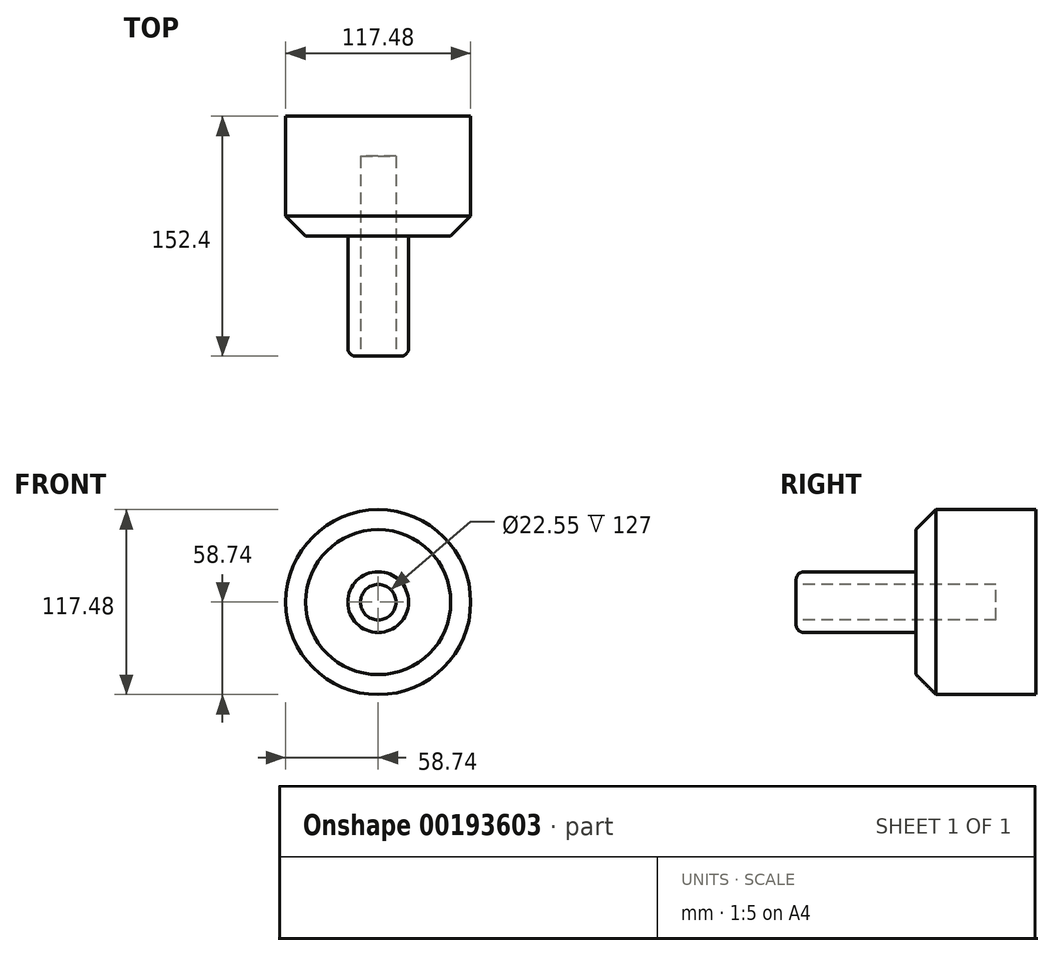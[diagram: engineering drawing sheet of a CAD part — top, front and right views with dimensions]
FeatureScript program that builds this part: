
annotation { "Feature Type Name" : "Feature", "Feature Type Description" : "" }
export const myFeature = defineFeature(function(context is Context, id is Id, definition is map)
    precondition{}
    {
        {
            var Q0;
            Q0=qCreatedBy(makeId("Front.planeOp"),FACE);
            var sketch = newSketch(context, id + "F0", { "sketchPlane" : qUnion([Q0])});
            skCircle(sketch, "E0", {"center": v(0, 0) * mm, "radius": 58.74 * mm});
            skSolve(sketch);
        }
        {
            var Q0;
            Q0=makeQuery(id+"F0.imprint","IMPRINT",FACE,{"disambiguationData":[TD([[makeQuery(id+"F0.imprint","IMPRINT",EDGE,{"derivedFrom":sQuery(id+"F0.wireOp",EDGE,"E0")}),1.0]])]});
            var sketch = newSketch(context, id + "F1", { "sketchPlane" : qUnion([Q0])});
            skSolve(sketch);
        }
        {
            var Q0;
            Q0 = qSketchRegion(id + "F1", true);
            var Q1;
            Q1=makeQuery(id+"F0.imprint","IMPRINT",FACE,{"disambiguationData":[TD([[makeQuery(id+"F0.imprint","IMPRINT",EDGE,{"derivedFrom":sQuery(id+"F0.wireOp",EDGE,"E0")}),1.0]])]});
            extrude(context, id + "F2", {"entities" : qUnion([Q0, Q1]), "depth" : 76.2 * mm});
        }
        {
            var Q0;
            Q0=makeQuery(id+"F2.opExtrude","CAP_FACE",FACE,{"disambiguationData":[OSD([sQuery(id+"F0.wireOp",EDGE,"E0")])],"isStart":false});
            var sketch = newSketch(context, id + "F3", { "sketchPlane" : qUnion([Q0])});
            skCircle(sketch, "E1", {"center": v(0, 0) * mm, "radius": 19.3 * mm});
            skSolve(sketch);
        }
        {
            var Q0;
            Q0=makeQuery(id+"F3.imprint","IMPRINT",FACE,{"disambiguationData":[TD([[makeQuery(id+"F3.imprint","IMPRINT",EDGE,{"derivedFrom":sQuery(id+"F3.wireOp",EDGE,"E1")}),1.0]])]});
            extrude(context, id + "F4", {"entities" : qUnion([Q0]), "operationType" : NewBodyOperationType.ADD, "depth" : 76.2 * mm});
        }
        {
            var Q0;
            Q0=qCreatedBy(makeId("Front.planeOp"),FACE);
            var sketch = newSketch(context, id + "F5", { "sketchPlane" : qUnion([Q0])});
            skCircle(sketch, "E2", {"center": v(0, 0) * mm, "radius": 9.66 * mm});
            skSolve(sketch);
        }
        {
            var Q0;
            Q0=qCreatedBy(makeId("Front.planeOp"),FACE);
            var sketch = newSketch(context, id + "F6", { "sketchPlane" : qUnion([Q0])});
            skCircle(sketch, "E3", {"center": v(0, 0) * mm, "radius": 9.7 * mm});
            skSolve(sketch);
        }
        {
            var Q0;
            Q0 = qSketchRegion(id + "F6", true);
            extrude(context, id + "F7", {"entities" : qUnion([Q0]), "operationType" : NewBodyOperationType.REMOVE, "oppositeDirection" : true, "depth" : 76.2 * mm});
        }
        {
            var Q0;
            Q0=makeQuery(id+"F5.imprint","IMPRINT",FACE,{"disambiguationData":[TD([[makeQuery(id+"F5.imprint","IMPRINT",EDGE,{"derivedFrom":sQuery(id+"F5.wireOp",EDGE,"E2")}),1.0]])]});
            var Q1;
            Q1=sQuery(id+"F5.wireOp",EDGE,"E2");
            extrude(context, id + "F8", {"entities" : qUnion([Q0]), "operationType" : NewBodyOperationType.REMOVE, "surfaceEntities" : qUnion([Q1]), "oppositeDirection" : true, "depth" : 127 * mm});
        }
        {
            var Q0;
            Q0=makeQuery(id+"F4.opExtrude","CAP_FACE",FACE,{"disambiguationData":[OSD([sQuery(id+"F3.wireOp",EDGE,"E1")])],"isStart":false});
            var sketch = newSketch(context, id + "F9", { "sketchPlane" : qUnion([Q0])});
            skCircle(sketch, "E4", {"center": v(0, 0) * mm, "radius": 11.27 * mm});
            skSolve(sketch);
        }
        {
            var Q0;
            Q0=makeQuery(id+"F9.imprint","IMPRINT",FACE,{"disambiguationData":[TD([[makeQuery(id+"F9.imprint","IMPRINT",EDGE,{"derivedFrom":sQuery(id+"F9.wireOp",EDGE,"E4")}),1.0]])]});
            var Q1;
            Q1=sQuery(id+"F9.wireOp",EDGE,"E4");
            extrude(context, id + "F10", {"entities" : qUnion([Q0]), "operationType" : NewBodyOperationType.REMOVE, "surfaceEntities" : qUnion([Q1]), "oppositeDirection" : true, "depth" : 127 * mm});
        }
        {
            var Q0;
            Q0=makeQuery(id+"F4.opExtrude","CAP_EDGE",EDGE,{"disambiguationData":[OSD([sQuery(id+"F3.wireOp",EDGE,"E1")])],"isStart":false});
            fillet(context, id + "F11", {"entities" : qUnion([Q0]), "radius" : 5.08 * mm, "tangentPropagation" : true, "allowEdgeOverflow" : false});
        }
        {
            var Q0;
            Q0=makeQuery(id+"F2.opExtrude","CAP_EDGE",EDGE,{"disambiguationData":[OSD([sQuery(id+"F0.wireOp",EDGE,"E0")])],"isStart":false});
            chamfer(context, id + "F12", {"entities" : qUnion([Q0]), "width" : 12.7 * mm, "tangentPropagation" : true});
        }
    });
